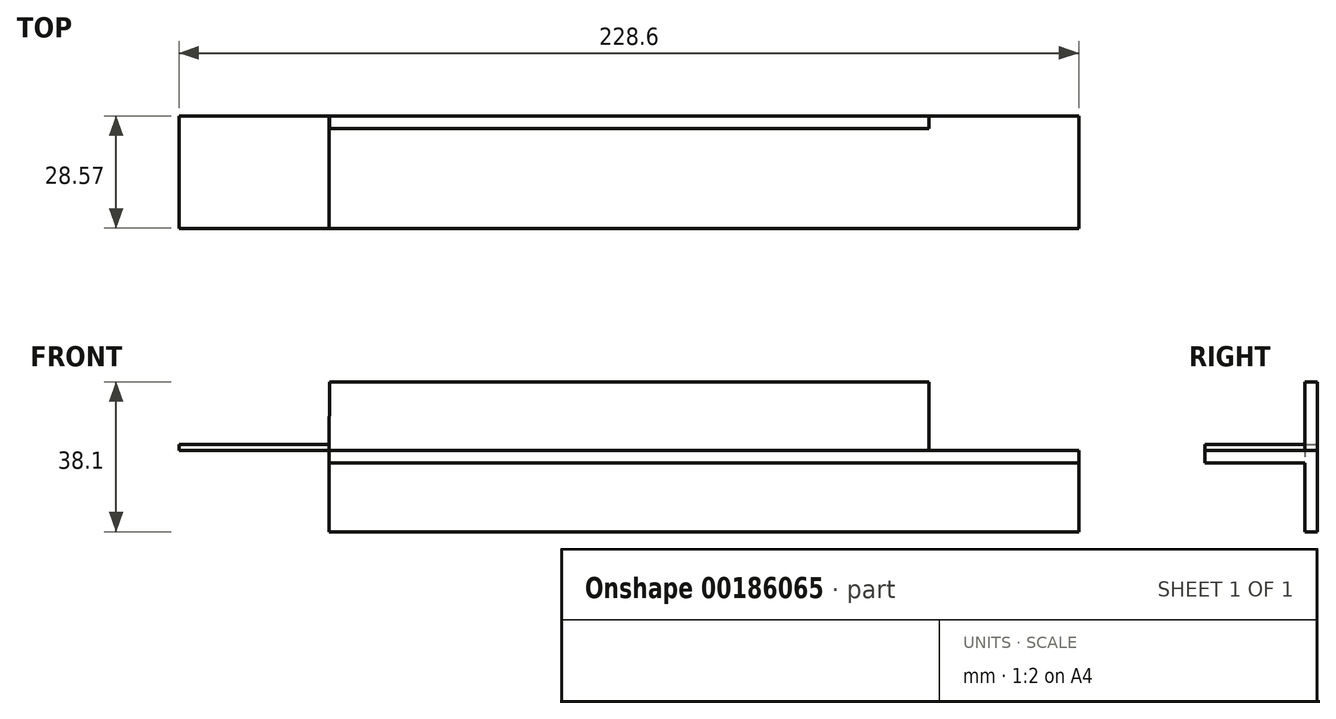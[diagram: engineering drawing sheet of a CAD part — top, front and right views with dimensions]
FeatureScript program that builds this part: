
annotation { "Feature Type Name" : "Feature", "Feature Type Description" : "" }
export const myFeature = defineFeature(function(context is Context, id is Id, definition is map)
    precondition{}
    {
        {
            var Q0;
            Q0=qCreatedBy(makeId("Front.planeOp"),FACE);
            var sketch = newSketch(context, id + "F0", { "sketchPlane" : qUnion([Q0])});
            skLineSegment(sketch, "E0.bottom", {"start": v(95.25, -19.05) * mm, "end": v(-95.25, -19.05) * mm});
            skLineSegment(sketch, "E0.top", {"start": v(95.25, 19.05) * mm, "end": v(-57.02, 19.05) * mm});
            skLineSegment(sketch, "E0.left", {"start": v(95.25, -19.05) * mm, "end": v(95.25, 19.05) * mm});
            skLineSegment(sketch, "E0.right", {"start": v(-95.25, -19.05) * mm, "end": v(-95.25, 0) * mm});
            skPoint(sketch, "E0.middle", {"position": v(0, 0) * mm});
            skLineSegment(sketch, "E1", {"start": v(0, 0) * mm, "end": v(95.25, 0) * mm});
            skLineSegment(sketch, "E2", {"start": v(95.25, 0) * mm, "end": v(-95.25, 0) * mm});
            skLineSegment(sketch, "E3", {"start": v(-57.02, 19.05) * mm, "end": v(-95.12, 19.05) * mm});
            skLineSegment(sketch, "E4", {"start": v(-95.12, 19.05) * mm, "end": v(-95.25, 0) * mm});
            skSolve(sketch);
        }
        {
            var Q0;
            {var subQ5=sQuery(id+"F0.wireOp",EDGE,"E0.bottom");Q0=makeQuery(id+"F0.imprint","IMPRINT",FACE,{"disambiguationData":[TD([[makeQuery(id+"F0.imprint","IMPRINT",EDGE,{"derivedFrom":subQ5}),-1.0]])]});}
            var Q1;
            {var subQ5=sQuery(id+"F0.wireOp",EDGE,"E0.top");Q1=makeQuery(id+"F0.imprint","IMPRINT",FACE,{"disambiguationData":[TD([[makeQuery(id+"F0.imprint","IMPRINT",EDGE,{"derivedFrom":subQ5}),1.0]])]});}
            extrude(context, id + "F1", {"entities" : qUnion([Q0, Q1]), "depth" : 3.17 * mm});
        }
        {
            var Q0;
            Q0=makeQuery(id+"F1.opExtrude","CAP_FACE",FACE,{"disambiguationData":[OSD([sQuery(id+"F0.wireOp",EDGE,"E0.bottom"),sQuery(id+"F0.wireOp",EDGE,"E0.top"),sQuery(id+"F0.wireOp",EDGE,"E0.left"),sQuery(id+"F0.wireOp",EDGE,"E0.right"),sQuery(id+"F0.wireOp",EDGE,"E2"),sQuery(id+"F0.wireOp",EDGE,"8UghfC07-c70b-QwZe-9ilX-imAFtbyGwoo4")])],"isStart":false});
            var sketch = newSketch(context, id + "F2", { "sketchPlane" : qUnion([Q0])});
            skLineSegment(sketch, "E5.bottom", {"start": v(-95.25, 0) * mm, "end": v(95.25, 0) * mm});
            skLineSegment(sketch, "E5.top", {"start": v(-95.25, 1.59) * mm, "end": v(95.25, 1.59) * mm});
            skLineSegment(sketch, "E5.left", {"start": v(-95.25, 0) * mm, "end": v(-95.25, 1.59) * mm});
            skLineSegment(sketch, "E5.right", {"start": v(95.25, 0) * mm, "end": v(95.25, 1.59) * mm});
            skLineSegment(sketch, "E6.bottom", {"start": v(95.25, 0) * mm, "end": v(-95.25, 0) * mm});
            skLineSegment(sketch, "E6.top", {"start": v(95.25, -1.59) * mm, "end": v(-95.25, -1.59) * mm});
            skLineSegment(sketch, "E6.left", {"start": v(95.25, 0) * mm, "end": v(95.25, -1.59) * mm});
            skLineSegment(sketch, "E6.right", {"start": v(-95.25, 0) * mm, "end": v(-95.25, -1.59) * mm});
            skSolve(sketch);
        }
        {
            var Q0;
            Q0 = qSketchRegion(id + "F2", true);
            extrude(context, id + "F3", {"entities" : qUnion([Q0]), "operationType" : NewBodyOperationType.ADD, "depth" : 25.4 * mm});
        }
        {
            var Q0;
            Q0=makeQuery(id+"F3.boolean.opBoolean","MERGE",FACE,{"derivedFrom":[makeQuery(id+"F1.opExtrude","SWEPT_FACE",FACE,{"disambiguationData":[OSD([sQuery(id+"F0.wireOp",EDGE,"8UghfC07-c70b-QwZe-9ilX-imAFtbyGwoo4")])]}),makeQuery(id+"F3.opExtrude","SWEPT_FACE",FACE,{"disambiguationData":[OSD([sQuery(id+"F2.wireOp",EDGE,"E5.left")])]})]});
            var sketch = newSketch(context, id + "F4", { "sketchPlane" : qUnion([Q0])});
            skLineSegment(sketch, "E7.bottom", {"start": v(28.58, 1.59) * mm, "end": v(0, 1.59) * mm});
            skLineSegment(sketch, "E7.top", {"start": v(28.58, 3.18) * mm, "end": v(0, 3.17) * mm});
            skLineSegment(sketch, "E7.left", {"start": v(28.58, 1.59) * mm, "end": v(28.58, 3.18) * mm});
            skLineSegment(sketch, "E7.right", {"start": v(0, 1.59) * mm, "end": v(0, 3.17) * mm});
            skSolve(sketch);
        }
        {
            var Q0;
            Q0 = qSketchRegion(id + "F4", true);
            extrude(context, id + "F5", {"entities" : qUnion([Q0]), "operationType" : NewBodyOperationType.ADD, "depth" : 38.1 * mm});
        }
        {
            var Q0;
            {var subQ1=sQuery(id+"F0.wireOp",EDGE,"E4");var subQ2=sQuery(id+"F0.wireOp",EDGE,"E0.left");var subQ5=sQuery(id+"F0.wireOp",EDGE,"E3");var subQ6=sQuery(id+"F0.wireOp",EDGE,"E0.top");Q0=makeQuery(id+"F3.boolean.opBoolean","SPLIT",FACE,{"disambiguationData":[TD([makeQuery(id+"F1.opExtrude","SWEPT_FACE",FACE,{"disambiguationData":[OSD([subQ1])]})])],"derivedFrom":makeQuery(id+"F1.opExtrude","CAP_FACE",FACE,{"disambiguationData":[OSD([sQuery(id+"F0.wireOp",EDGE,"E0.bottom"),subQ6,subQ2,sQuery(id+"F0.wireOp",EDGE,"E0.right"),subQ5,subQ1])],"isStart":false})});}
            var sketch = newSketch(context, id + "F6", { "sketchPlane" : qUnion([Q0])});
            skLineSegment(sketch, "E8", {"start": v(57.15, 19.05) * mm, "end": v(57.15, 1.59) * mm});
            skSolve(sketch);
        }
        {
            var Q0;
            {var subQ0=sQuery(id+"F6.wireOp",EDGE,"E8");Q0=makeQuery(id+"F6.imprint","IMPRINT",FACE,{"disambiguationData":[TD([[makeQuery(id+"F6.imprint","IMPRINT",EDGE,{"derivedFrom":subQ0}),1.0]])]});}
            extrude(context, id + "F7", {"entities" : qUnion([Q0]), "operationType" : NewBodyOperationType.REMOVE, "oppositeDirection" : true, "depth" : 25.4 * mm});
        }
    });
